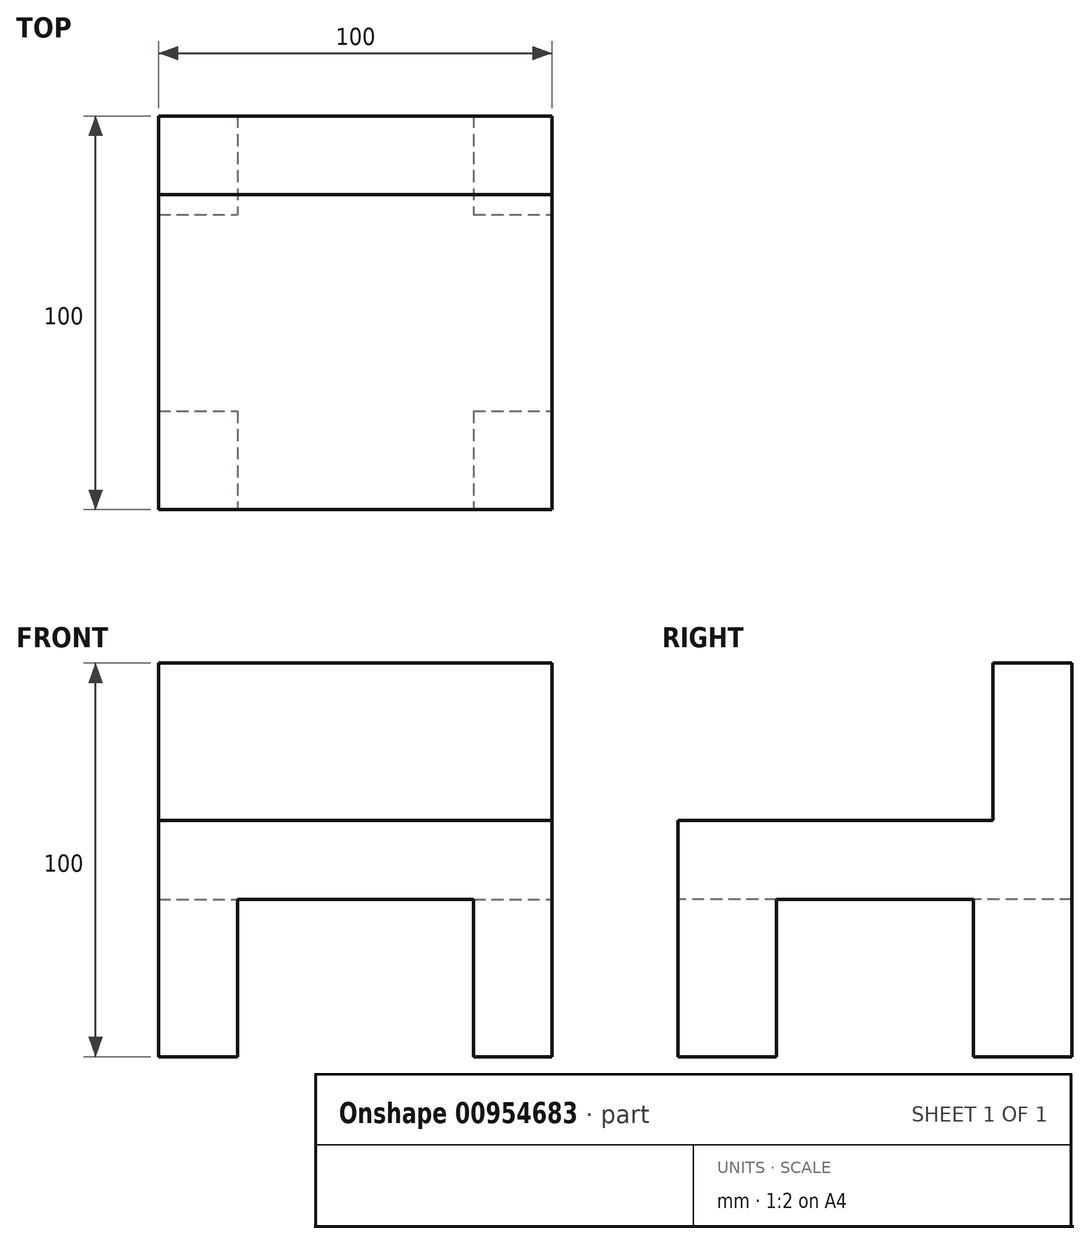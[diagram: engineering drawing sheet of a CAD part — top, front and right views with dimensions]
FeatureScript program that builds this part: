
annotation { "Feature Type Name" : "Feature", "Feature Type Description" : "" }
export const myFeature = defineFeature(function(context is Context, id is Id, definition is map)
    precondition{}
    {
        {
            var Q0;
            Q0=qCreatedBy(makeId("Top.planeOp"),FACE);
            var sketch = newSketch(context, id + "F0", { "sketchPlane" : qUnion([Q0])});
            skLineSegment(sketch, "E0.bottom", {"start": v(-50, -50) * mm, "end": v(50, -50) * mm});
            skLineSegment(sketch, "E0.top", {"start": v(-50, 50) * mm, "end": v(50, 50) * mm});
            skLineSegment(sketch, "E0.left", {"start": v(-50, -50) * mm, "end": v(-50, 50) * mm});
            skLineSegment(sketch, "E0.right", {"start": v(50, -50) * mm, "end": v(50, 50) * mm});
            skPoint(sketch, "E0.middle", {"position": v(0, 0) * mm});
            skSolve(sketch);
        }
        {
            var Q0;
            Q0=makeQuery(id+"F0.imprint","IMPRINT",FACE,{"disambiguationData":[TD([[makeQuery(id+"F0.imprint","IMPRINT",EDGE,{"derivedFrom":sQuery(id+"F0.wireOp",EDGE,"E0.bottom")}),1.0]])]});
            extrude(context, id + "F1", {"entities" : qUnion([Q0]), "depth" : 100 * mm, "offsetDistance" : 25 * mm});
        }
        {
            var Q0;
            Q0=makeQuery(id+"F1.opExtrude","CAP_FACE",FACE,{"disambiguationData":[OSD([sQuery(id+"F0.wireOp",EDGE,"E0.bottom"),sQuery(id+"F0.wireOp",EDGE,"E0.top"),sQuery(id+"F0.wireOp",EDGE,"E0.left"),sQuery(id+"F0.wireOp",EDGE,"E0.right")])],"isStart":false});
            var sketch = newSketch(context, id + "F2", { "sketchPlane" : qUnion([Q0])});
            skLineSegment(sketch, "E1.bottom", {"start": v(50, -50) * mm, "end": v(-50, -50) * mm});
            skLineSegment(sketch, "E1.top", {"start": v(50, 30) * mm, "end": v(-50, 30) * mm});
            skLineSegment(sketch, "E1.left", {"start": v(50, -50) * mm, "end": v(50, 30) * mm});
            skLineSegment(sketch, "E1.right", {"start": v(-50, -50) * mm, "end": v(-50, 30) * mm});
            skSolve(sketch);
        }
        {
            var Q0;
            Q0=makeQuery(id+"F2.imprint","IMPRINT",FACE,{"disambiguationData":[TD([[makeQuery(id+"F2.imprint","IMPRINT",EDGE,{"derivedFrom":sQuery(id+"F2.wireOp",EDGE,"E1.bottom")}),1.0]])]});
            extrude(context, id + "F3", {"entities" : qUnion([Q0]), "operationType" : NewBodyOperationType.REMOVE, "oppositeDirection" : true, "depth" : 40 * mm, "offsetDistance" : 25 * mm});
        }
        {
            var Q0;
            Q0=makeQuery(id+"F1.opExtrude","SWEPT_FACE",FACE,{"disambiguationData":[OSD([sQuery(id+"F0.wireOp",EDGE,"E0.bottom")])]});
            var sketch = newSketch(context, id + "F4", { "sketchPlane" : qUnion([Q0])});
            skLineSegment(sketch, "E2.bottom", {"start": v(-30, 0) * mm, "end": v(30, 0) * mm});
            skLineSegment(sketch, "E2.top", {"start": v(-30, 40) * mm, "end": v(30, 40) * mm});
            skLineSegment(sketch, "E2.left", {"start": v(-30, 0) * mm, "end": v(-30, 40) * mm});
            skLineSegment(sketch, "E2.right", {"start": v(30, 0) * mm, "end": v(30, 40) * mm});
            skSolve(sketch);
        }
        {
            var Q0;
            Q0=makeQuery(id+"F4.imprint","IMPRINT",FACE,{"disambiguationData":[TD([[makeQuery(id+"F4.imprint","IMPRINT",EDGE,{"derivedFrom":sQuery(id+"F4.wireOp",EDGE,"E2.bottom")}),1.0]])]});
            extrude(context, id + "F5", {"entities" : qUnion([Q0]), "operationType" : NewBodyOperationType.REMOVE, "endBound" : BoundingType.THROUGH_ALL, "oppositeDirection" : true, "depth" : 25 * mm, "offsetDistance" : 25 * mm});
        }
        {
            var Q0;
            Q0=makeQuery(id+"F1.opExtrude","SWEPT_FACE",FACE,{"disambiguationData":[OSD([sQuery(id+"F0.wireOp",EDGE,"E0.right")])]});
            var sketch = newSketch(context, id + "F6", { "sketchPlane" : qUnion([Q0])});
            skLineSegment(sketch, "E3.bottom", {"start": v(-25, 0) * mm, "end": v(25, 0) * mm});
            skLineSegment(sketch, "E3.top", {"start": v(-25, 40) * mm, "end": v(25, 40) * mm});
            skLineSegment(sketch, "E3.left", {"start": v(-25, 0) * mm, "end": v(-25, 40) * mm});
            skLineSegment(sketch, "E3.right", {"start": v(25, 0) * mm, "end": v(25, 40) * mm});
            skSolve(sketch);
        }
        {
            var Q0;
            Q0 = qSketchRegion(id + "F6", true);
            extrude(context, id + "F7", {"entities" : qUnion([Q0]), "operationType" : NewBodyOperationType.REMOVE, "endBound" : BoundingType.THROUGH_ALL, "oppositeDirection" : true, "depth" : 25 * mm, "offsetDistance" : 25 * mm});
        }
    });
